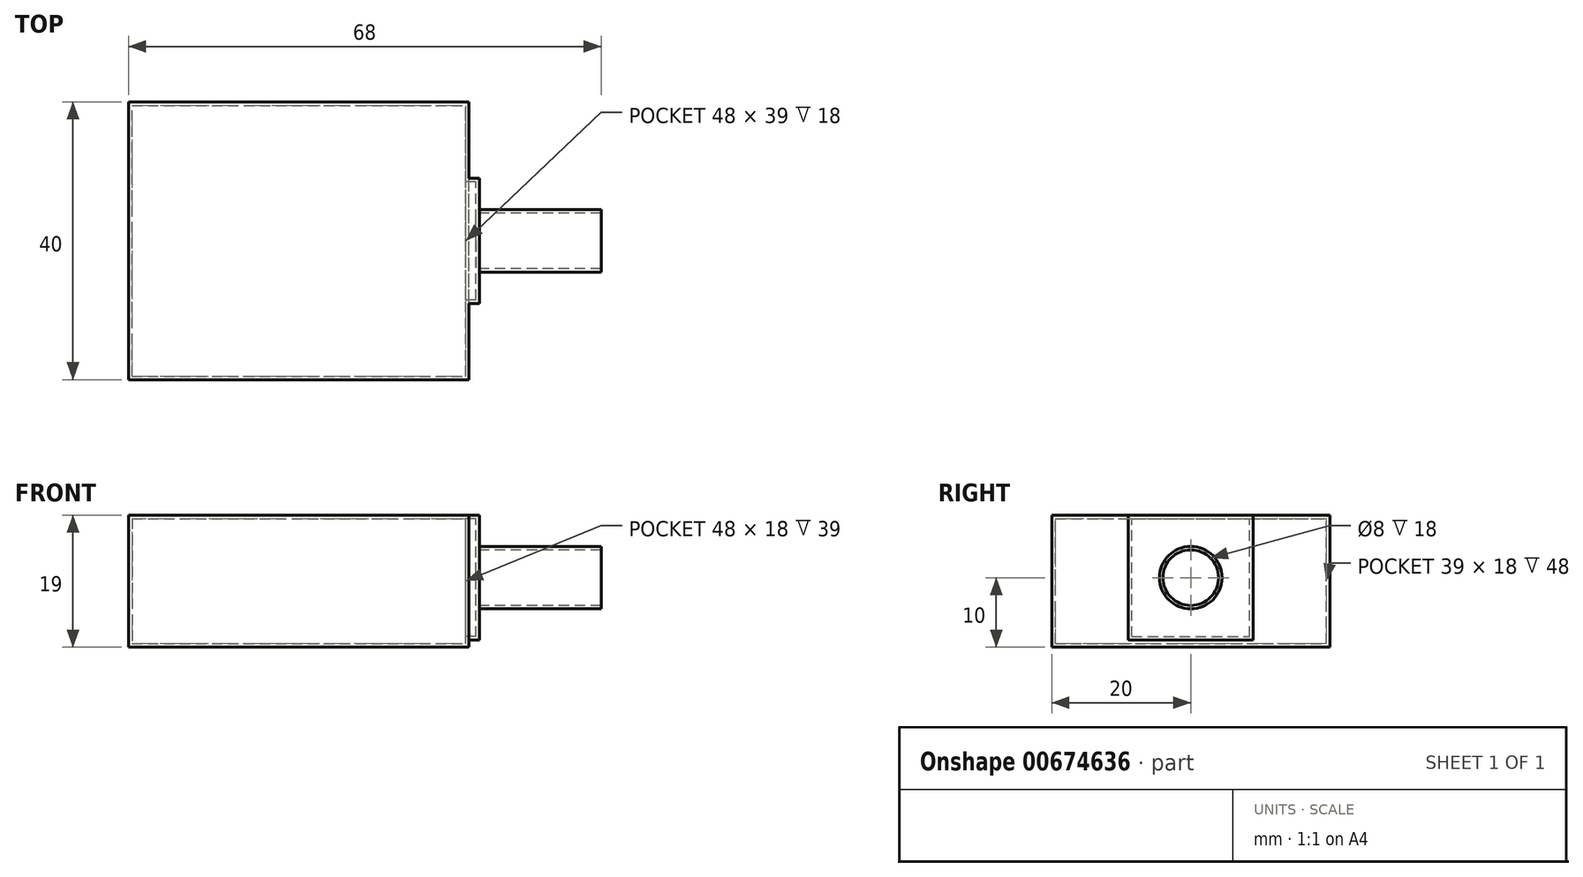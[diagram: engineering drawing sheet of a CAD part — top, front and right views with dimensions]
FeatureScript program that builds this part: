
annotation { "Feature Type Name" : "Feature", "Feature Type Description" : "" }
export const myFeature = defineFeature(function(context is Context, id is Id, definition is map)
    precondition{}
    {
        {
            var Q0;
            Q0=qCreatedBy(makeId("Front.planeOp"),FACE);
            var sketch = newSketch(context, id + "F0", { "sketchPlane" : qUnion([Q0])});
            skLineSegment(sketch, "E0", {"start": v(-23, 19) * mm, "end": v(26, 19) * mm});
            skLineSegment(sketch, "E1", {"start": v(-23, 19) * mm, "end": v(-23, 0) * mm});
            skLineSegment(sketch, "E2", {"start": v(-23, 0) * mm, "end": v(26, 0) * mm});
            skLineSegment(sketch, "E3", {"start": v(26, 0) * mm, "end": v(26, 19) * mm});
            skPoint(sketch, "E4", {"position": v(0, 0) * mm});
            skSolve(sketch);
        }
        {
            var Q0;
            Q0=makeQuery(id+"F0.imprint","IMPRINT",FACE,{"disambiguationData":[TD([[makeQuery(id+"F0.imprint","IMPRINT",EDGE,{"derivedFrom":sQuery(id+"F0.wireOp",EDGE,"E0")}),-1.0]])]});
            extrude(context, id + "F1", {"entities" : qUnion([Q0]), "depth" : 40 * mm, "offsetDistance" : 25 * mm, "symmetric" : true});
        }
        {
            var Q0;
            Q0=makeQuery(id+"F1.opExtrude","SWEPT_FACE",FACE,{"disambiguationData":[OSD([sQuery(id+"F0.wireOp",EDGE,"E3")])]});
            var sketch = newSketch(context, id + "F2", { "sketchPlane" : qUnion([Q0])});
            skLineSegment(sketch, "E5", {"start": v(-9, 1) * mm, "end": v(0, 1) * mm});
            skLineSegment(sketch, "E6", {"start": v(-9, 1) * mm, "end": v(-9, 19) * mm});
            skLineSegment(sketch, "E7", {"start": v(-9, 19) * mm, "end": v(0, 19) * mm});
            skLineSegment(sketch, "E8.MirrorCS", {"start": v(9, 19) * mm, "end": v(0, 19) * mm});
            skLineSegment(sketch, "E9.MirrorCS", {"start": v(9, 1) * mm, "end": v(9, 19) * mm});
            skLineSegment(sketch, "E10.MirrorCS", {"start": v(9, 1) * mm, "end": v(0, 1) * mm});
            skCircle(sketch, "E11", {"center": v(0, 10) * mm, "radius": 4.5 * mm});
            skPoint(sketch, "E12", {"position": v(-9, 10) * mm});
            skLineSegment(sketch, "E13", {"start": v(-9, 10) * mm, "end": v(9, 10) * mm, "construction": true});
            skSolve(sketch);
        }
        {
            var Q0;
            Q0=makeQuery(id+"F2.imprint","IMPRINT",FACE,{"disambiguationData":[TD([[makeQuery(id+"F2.imprint","IMPRINT",EDGE,{"derivedFrom":sQuery(id+"F2.wireOp",EDGE,"E5")}),1.0]])]});
            extrude(context, id + "F3", {"entities" : qUnion([Q0]), "operationType" : NewBodyOperationType.ADD, "depth" : 1.5 * mm, "offsetDistance" : 25 * mm});
        }
        {
            var Q0;
            Q0=makeQuery(id+"F3.boolean.opBoolean","SPLIT",FACE,{"disambiguationData":[TD([makeQuery(id+"F3.opExtrude","SWEPT_FACE",FACE,{"disambiguationData":[OSD([sQuery(id+"F2.wireOp",EDGE,"E11")])]})])],"derivedFrom":makeQuery(id+"F1.opExtrude","SWEPT_FACE",FACE,{"disambiguationData":[OSD([sQuery(id+"F0.wireOp",EDGE,"E3")])]})});
            extrude(context, id + "F4", {"entities" : qUnion([Q0]), "operationType" : NewBodyOperationType.ADD, "depth" : 19 * mm, "offsetDistance" : 25 * mm});
        }
        {
            var Q0;
            Q0=makeQuery(id+"F4.opExtrude","CAP_FACE",FACE,{"disambiguationData":[OSD([sQuery(id+"F0.wireOp",EDGE,"E3")])],"isStart":false});
            shell(context, id + "F5", {"entities" : qUnion([Q0]), "thickness" : .5 * mm});
        }
    });
